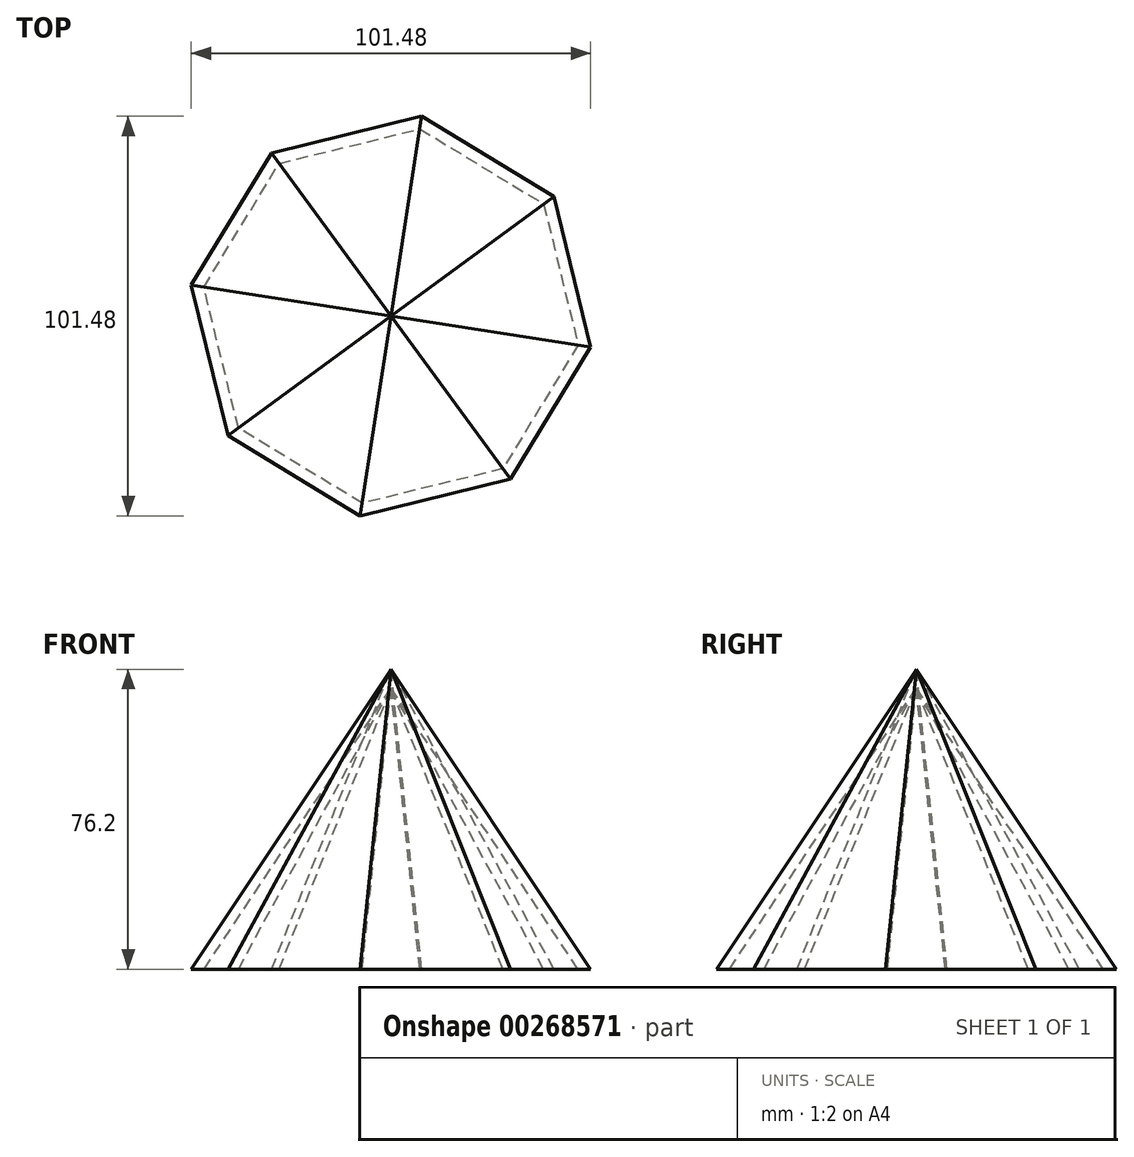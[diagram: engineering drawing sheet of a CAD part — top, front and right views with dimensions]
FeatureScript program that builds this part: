
annotation { "Feature Type Name" : "Feature", "Feature Type Description" : "" }
export const myFeature = defineFeature(function(context is Context, id is Id, definition is map)
    precondition{}
    {
        {
            var Q0;
            Q0=qCreatedBy(makeId("Top.planeOp"),FACE);
            var sketch = newSketch(context, id + "F0", { "sketchPlane" : qUnion([Q0])});
            skCircle(sketch, "E0.cCircle", {"center": v(0, 0) * mm, "radius": 47.43 * mm, "construction": true});
            skLineSegment(sketch, "E0.0", {"start": v(-50.74, 7.81) * mm, "end": v(-30.35, 41.4) * mm});
            skLineSegment(sketch, "E0.1", {"start": v(-30.35, 41.4) * mm, "end": v(7.81, 50.74) * mm});
            skLineSegment(sketch, "E0.2", {"start": v(7.81, 50.74) * mm, "end": v(41.4, 30.35) * mm});
            skLineSegment(sketch, "E0.3", {"start": v(41.4, 30.35) * mm, "end": v(50.74, -7.81) * mm});
            skLineSegment(sketch, "E0.4", {"start": v(50.74, -7.81) * mm, "end": v(30.35, -41.4) * mm});
            skLineSegment(sketch, "E0.5", {"start": v(30.35, -41.4) * mm, "end": v(-7.81, -50.74) * mm});
            skLineSegment(sketch, "E0.6", {"start": v(-7.81, -50.74) * mm, "end": v(-41.4, -30.35) * mm});
            skLineSegment(sketch, "E0.7", {"start": v(-41.4, -30.35) * mm, "end": v(-50.74, 7.81) * mm});
            skPoint(sketch, "E0.0.midPoint", {"position": v(-40.55, 24.6) * mm});
            skSolve(sketch);
        }
        {
            var Q0;
            Q0=qCreatedBy(makeId("Top.planeOp"),FACE);
            cPlane(context, id + "F1", {"entities" : qUnion([Q0]), "cplaneType" : CPlaneType.OFFSET, "offset" : 76.2 * mm, "width" : 152.4 * mm, "height" : 152.4 * mm});
        }
        {
            var Q0;
            Q0=qCreatedBy(id+"F1.planeOp",FACE);
            var sketch = newSketch(context, id + "F2", { "sketchPlane" : qUnion([Q0])});
            skPoint(sketch, "E1", {"position": v(0, 0) * mm});
            skSolve(sketch);
        }
        {
            var Q0;
            Q0=makeQuery(id+"F0.imprint","IMPRINT",FACE,{"disambiguationData":[TD([[makeQuery(id+"F0.imprint","IMPRINT",EDGE,{"derivedFrom":sQuery(id+"F0.wireOp",EDGE,"E0.0")}),-1.0]])]});
            var Q1;
            Q1=sQuery(id+"F2.wireOp",VERTEX,"E1");
            loft(context, id + "F3", {"sheetProfilesArray" : [{ "sheetProfileEntities" : qUnion([Q0]) }, { "sheetProfileEntities" : qUnion([Q1]) }]});
        }
        {
            var Q0;
            Q0=makeQuery(id+"F3.opLoft","CAP_FACE",FACE,{"disambiguationData":[OSD([makeQuery(id+"F0.imprint","IMPRINT",FACE,{"disambiguationData":[TD([[makeQuery(id+"F0.imprint","IMPRINT",EDGE,{"derivedFrom":sQuery(id+"F0.wireOp",EDGE,"E0.0")}),-1.0]])]})])],"isStart":true});
            shell(context, id + "F4", {"entities" : qUnion([Q0]), "thickness" : 2.54 * mm});
        }
    });
